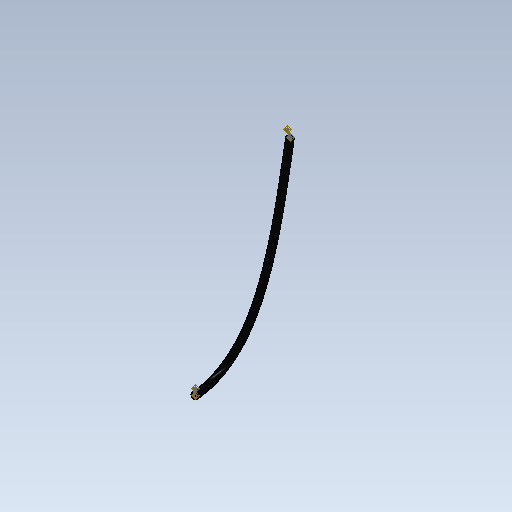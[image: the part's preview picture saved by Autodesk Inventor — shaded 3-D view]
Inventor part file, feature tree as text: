
AUTODESK INVENTOR PART (.ipt)
format: ipt  version: 2020 (Build 240168000, 168)  size: 105,984 bytes
history: native  units: mm (DEFAULTED — no unit token found)
features: other x16, plane x1, sketch x1
bodies: Body1 (feature_tree)
feature tree (18):
  other  "Origen"
  other  "Punto de trabajo1"
  other  "Punto de trabajo2"
  other  "Conductor1"
  other  "Punto de trabajo3"
  other  "Punto de trabajo4"
  other  "Segmento1"
  other  "Punto de trabajo5"
  plane  "Plano de trabajo1"
  other  "Plano YZ"
  other  "Plano XZ"
  other  "Plano XY"
  other  "Eje X"
  other  "Eje Y"
  other  "Eje Z"
  sketch  "Boceto1"  dims[d0=0.0mm d1=0.0mm]
  other  "Sup1"
  other  "SuperficieBarrido1"
